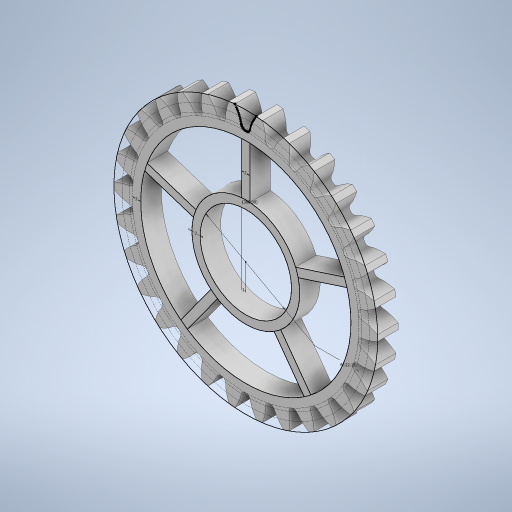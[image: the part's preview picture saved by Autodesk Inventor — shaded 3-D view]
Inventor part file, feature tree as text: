
AUTODESK INVENTOR PART (.ipt)
format: ipt  version: 2023 (Build 270158000, 158)  size: 492,032 bytes
history: native  units: mm
features: extrude x2, sketch x1, pattern_circular x1
ambient origin geometry x8: Origin, YZ Plane, XZ Plane, XY Plane, X Axis, Y Axis, Z Axis, Center Point
bodies: Solid1 (feature_tree)
feature tree (4):
  sketch  "Sketch1"  dims[d0=5.0mm d1=0.0mm d2=2.0mm d3=22.15mm d4=2.0mm d5=1.0mm d6=2.0mm d7=50.0mm d9=360.0deg d11=0.0mm d12=0.0mm d13=300.0mm d14=360.0deg]
  extrude  "Extrusion1"  TaperAngle=0.0deg  [1 undecoded]
  extrude  "Extrusion2"  Depth=2.0mm
  pattern_circular  "Circular Pattern1"  [2 undecoded]
note: 3 required parameter values undecoded (feature->parameter linkage not recoverable at this tier; creation-order binding heuristic only, values carry confidence <= 0.55)
